# Revit family: Thorn KATONA Square
name_source: partatom
category: Lighting Fixtures
revit_build: Autodesk Revit 2016 (Build: 20150220_1215(x64)
units: mm (PartAtom-declared; Revit-internal decimal feet)

## family parameters
Cut with Voids When Loaded = No
Host = Face
Light Source = Yes
OmniClass Number = 23.80.70.11
OmniClass Title = Luminaries for Internal Lighting
Part Type = Normal
Room Calculation Point = No
Round Connector Dimension = Use Diameter
Shared = No

## types (3) — shared parameters
Assembly Code = D5020200
Body = Thorn_Metal_White
Color Filter = 16777215
Cover = Thorn_PMMA
Description = Square wall mounted LED
Dimming Lamp Color Temperature Shift = <None>
Emit Shape Visible in Rendering = No
Emit from Rectangle Length = 211 mm  [stored 0.692257 ft]
Emit from Rectangle Width = 211 mm  [stored 0.692257 ft]
Height = 58 mm  [stored 0.190289 ft]
Lamp = LED
Length = 277 mm  [stored 0.908793 ft]
Manufacturer = Thorn Lighting
Tilt Angle = -90.00°
Voltage = 230 V
Width = 277 mm  [stored 0.908793 ft]
zero-valued in all types: Default Elevation

## per-type parameters (varying)
| type | Apparent Load | Model | Photometric Web File | URL |
| KAT SQ 1000lm | 8 VA | 96629368 | TLG_SP_0043590.IES | www.thornlighting.com/96629368 |
| KAT SQ 1400lm | 12 VA | 96631331 | TLG_SP_0043592.IES | www.thornlighting.com/96631331 |
| KAT SQ 2000lm | 12 VA | 96629370 | TLG_SP_0043594.IES | www.thornlighting.com/96629370 |

note: [stored X ft] marks values corroborated as IEEE doubles in the binary element streams (Revit-internal decimal feet)

## geometry (parser evidence)
native form markers: Sweep x3
no freeform markers — native parametric forms only
